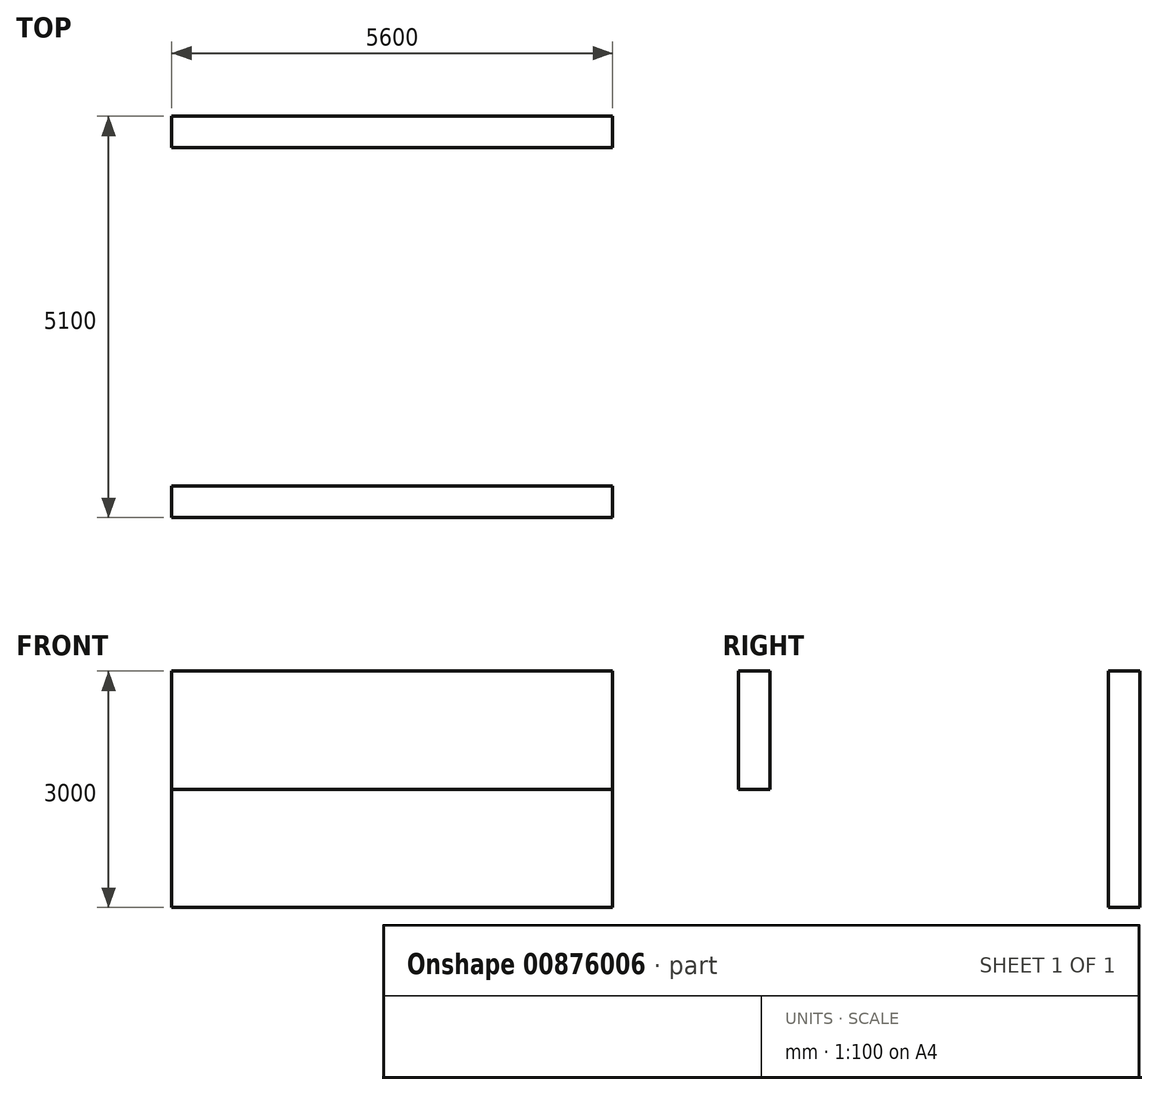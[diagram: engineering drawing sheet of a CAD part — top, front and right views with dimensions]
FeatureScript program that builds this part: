
annotation { "Feature Type Name" : "Feature", "Feature Type Description" : "" }
export const myFeature = defineFeature(function(context is Context, id is Id, definition is map)
    precondition{}
    {
        {
            var Q0;
            Q0=qCreatedBy(makeId("Top.planeOp"),FACE);
            var sketch = newSketch(context, id + "F0", { "sketchPlane" : qUnion([Q0])});
            skLineSegment(sketch, "E0", {"start": v(0, 0) * mm, "end": v(0, 5000) * mm});
            skLineSegment(sketch, "E1.bottom", {"start": v(-1500, 2550) * mm, "end": v(-7100, 2550) * mm});
            skLineSegment(sketch, "E1.top", {"start": v(-1500, -2550) * mm, "end": v(-7100, -2550) * mm});
            skLineSegment(sketch, "E1.left", {"start": v(-1500, 2550) * mm, "end": v(-1500, -2550) * mm});
            skLineSegment(sketch, "E1.right", {"start": v(-7100, 2550) * mm, "end": v(-7100, -2550) * mm});
            skLineSegment(sketch, "E2", {"start": v(0, 0) * mm, "end": v(0, -5000) * mm});
            skPoint(sketch, "E3", {"position": v(-1500, 0) * mm});
            skLineSegment(sketch, "E4", {"start": v(0, 0) * mm, "end": v(-8000, 0) * mm, "construction": true});
            skLineSegment(sketch, "E5", {"start": v(-7100, 2150) * mm, "end": v(-1500, 2150) * mm});
            skLineSegment(sketch, "E6", {"start": v(-7100, -2150) * mm, "end": v(-1500, -2150) * mm});
            skLineSegment(sketch, "E7", {"start": v(-3000, 2755) * mm, "end": v(-9573.95, 2755) * mm, "construction": true});
            skLineSegment(sketch, "E8", {"start": v(-3000, 2755) * mm, "end": v(-3000, 8624.5) * mm, "construction": true});
            skText(sketch, "E9", { "text": "Haus", "fontName": "OpenSans-Regular.ttf"});
            skLineSegment(sketch, "E10", {"start": v(-3000, 2755) * mm, "end": v(0, 2755) * mm, "construction": true});
            const initialGuessF0  = {"E9": [-6.08709, 3.80554, 1, 0, 0.54184]};
            skSetInitialGuess(sketch, initialGuessF0);
            skSolve(sketch);
        }
        {
            var Q0;
            {var subQ0=sQuery(id+"F0.wireOp",EDGE,"E1.top");Q0=makeQuery(id+"F0.imprint","IMPRINT",FACE,{"disambiguationData":[TD([[makeQuery(id+"F0.imprint","IMPRINT",EDGE,{"derivedFrom":subQ0}),-1.0]])]});}
            extrude(context, id + "F1", {"entities" : qUnion([Q0]), "oppositeDirection" : true, "depth" : 1500 * mm, "offsetDistance" : 25 * mm});
        }
        {
            var Q0;
            {var subQ0=sQuery(id+"F0.wireOp",EDGE,"E1.bottom");Q0=makeQuery(id+"F0.imprint","IMPRINT",FACE,{"disambiguationData":[TD([[makeQuery(id+"F0.imprint","IMPRINT",EDGE,{"derivedFrom":subQ0}),1.0]])]});}
            extrude(context, id + "F2", {"entities" : qUnion([Q0]), "oppositeDirection" : true, "depth" : 3000 * mm, "offsetDistance" : 25 * mm});
        }
        {
            var Q0;
            Q0=qCreatedBy(makeId("Right.planeOp"),FACE);
            var sketch = newSketch(context, id + "F3", { "sketchPlane" : qUnion([Q0])});
            skLineSegment(sketch, "E11", {"start": v(2755, 0) * mm, "end": v(2755, 325) * mm, "construction": true});
            skLineSegment(sketch, "E12", {"start": v(-2650, 0) * mm, "end": v(-2650, 175) * mm, "construction": true});
            skLineSegment(sketch, "E13", {"start": v(-2650, 175) * mm, "end": v(2755, 325) * mm});
            skPoint(sketch, "E14.0", {"position": v(-2550, 0) * mm});
            skLineSegment(sketch, "E15", {"start": v(-2550, 0) * mm, "end": v(-2550, 177.78) * mm, "construction": true});
            skLineSegment(sketch, "E16", {"start": v(0, 0) * mm, "end": v(0, 248.54) * mm, "construction": true});
            skLineSegment(sketch, "E17", {"start": v(0, 248.54) * mm, "end": v(0, 3048.54) * mm, "construction": true});
            skPoint(sketch, "E18.0", {"position": v(2550, 0) * mm});
            skLineSegment(sketch, "E19", {"start": v(2550, 0) * mm, "end": v(2550, 3500) * mm, "construction": true});
            skSolve(sketch);
        }
        {
            var Q0;
            Q0=makeQuery(id+"F2.opExtrude","SWEPT_FACE",FACE,{"disambiguationData":[OSD([sQuery(id+"F0.wireOp",EDGE,"E1.left")])]});
            var sketch = newSketch(context, id + "F4", { "sketchPlane" : qUnion([Q0])});
            skLineSegment(sketch, "E20", {"start": v(2550, 0) * mm, "end": v(2550, 400) * mm});
            skLineSegment(sketch, "E21", {"start": v(-2650, 0) * mm, "end": v(-2650, 400) * mm});
            skLineSegment(sketch, "E22.0", {"start": v(2755, 0) * mm, "end": v(2755, 400) * mm, "construction": true});
            skPoint(sketch, "E23.orphan", {"position": v(2755, 325) * mm});
            skLineSegment(sketch, "E24", {"start": v(2755, 400) * mm, "end": v(-2650, 400) * mm});
            skSolve(sketch);
        }
        {
            var Q0;
            Q0=makeQuery(id+"F1.opExtrude","SWEPT_FACE",FACE,{"disambiguationData":[OSD([sQuery(id+"F0.wireOp",EDGE,"E1.top")])]});
            cPlane(context, id + "F5", {"entities" : qUnion([Q0]), "cplaneType" : CPlaneType.OFFSET, "offset" : 100 * mm, "width" : 150 * mm, "height" : 150 * mm});
        }
        {
            var Q0;
            Q0=qCreatedBy(id+"F5.planeOp",FACE);
            var sketch = newSketch(context, id + "F6", { "sketchPlane" : qUnion([Q0])});
            skPoint(sketch, "E25.0", {"position": v(0, 177.78) * mm});
            skLineSegment(sketch, "E26.0", {"start": v(-1500, 0) * mm, "end": v(-7100, 0) * mm, "construction": true});
            skLineSegment(sketch, "E27", {"start": v(-1500, 0) * mm, "end": v(1749.53, -40.62) * mm, "construction": true});
            skLineSegment(sketch, "E28", {"start": v(-7100, 0) * mm, "end": v(-12930.36, 0) * mm, "construction": true});
            skLineSegment(sketch, "E29", {"start": v(-1500, 0) * mm, "end": v(-1500, 350) * mm});
            skLineSegment(sketch, "E30", {"start": v(-1500, 350) * mm, "end": v(0, 177.78) * mm});
            skLineSegment(sketch, "E31", {"start": v(-7100, 0) * mm, "end": v(-7100, 550) * mm});
            skLineSegment(sketch, "E32", {"start": v(-7100, 550) * mm, "end": v(-1500, 350) * mm});
            skLineSegment(sketch, "E33", {"start": v(0, 177.78) * mm, "end": v(0, -18.75) * mm, "construction": true});
            skPoint(sketch, "E34", {"position": v(0, -18.75) * mm});
            skSolve(sketch);
        }
        {
            var Q0;
            Q0=sQuery(id+"F3.wireOp",VERTEX,"E11.end");
            var Q1;
            Q1=sQuery(id+"F0.wireOp",VERTEX,"E10.end");
            var Q2;
            Q2=sQuery(id+"F0.wireOp",VERTEX,"E7.end");
            cPlane(context, id + "F7", {"entities" : qUnion([Q0, Q1, Q2]), "cplaneType" : CPlaneType.THREE_POINT, "offset" : 25 * mm, "width" : 150 * mm, "height" : 150 * mm});
        }
        {
            var Q0;
            Q0=qCreatedBy(id+"F7.planeOp",FACE);
            var sketch = newSketch(context, id + "F8", { "sketchPlane" : qUnion([Q0])});
            skPoint(sketch, "E35.0", {"position": v(0, 325) * mm});
            skLineSegment(sketch, "E36.0", {"start": v(-7100, -3000) * mm, "end": v(-7100, 0) * mm, "construction": true});
            skLineSegment(sketch, "E37.0", {"start": v(-1500, -3000) * mm, "end": v(-1500, 0) * mm, "construction": true});
            skLineSegment(sketch, "E38", {"start": v(-7100, 0) * mm, "end": v(-7100, 550) * mm, "construction": true});
            skLineSegment(sketch, "E39", {"start": v(-1500, 0) * mm, "end": v(-1500, 400) * mm, "construction": true});
            skLineSegment(sketch, "E40", {"start": v(-1500, 400) * mm, "end": v(-7100, 550) * mm});
            skSolve(sketch);
        }
        {
            var Q0;
            Q0=sQuery(id+"F4.wireOp",VERTEX,"E21.end");
            var Q1;
            {var subQ0=sQuery(id+"F0.wireOp",EDGE,"E1.top");Q1=makeQuery(id+"F0.imprint","IMPRINT",FACE,{"disambiguationData":[TD([[makeQuery(id+"F0.imprint","IMPRINT",EDGE,{"derivedFrom":subQ0}),-1.0]])]});}
            cPlane(context, id + "F9", {"entities" : qUnion([Q0, Q1]), "cplaneType" : CPlaneType.PLANE_POINT, "offset" : 25 * mm, "width" : 150 * mm, "height" : 150 * mm});
        }
        {
            var Q0;
            Q0=qCreatedBy(id+"F9.planeOp",FACE);
            var sketch = newSketch(context, id + "F10", { "sketchPlane" : qUnion([Q0])});
            skPoint(sketch, "E41.0", {"position": v(-7100, -2550) * mm});
            skPoint(sketch, "E42.0", {"position": v(-7100, 2550) * mm});
            skPoint(sketch, "E43.0", {"position": v(-1500, 2550) * mm});
            skPoint(sketch, "E44.0", {"position": v(-1500, -2550) * mm});
            skLineSegment(sketch, "E45", {"start": v(-7100, -2550) * mm, "end": v(-1500, -2550) * mm});
            skLineSegment(sketch, "E46", {"start": v(-1500, 2550) * mm, "end": v(-7100, 2550) * mm});
            skLineSegment(sketch, "E47", {"start": v(-7100, -2550) * mm, "end": v(-7100, 2550) * mm});
            skLineSegment(sketch, "E48", {"start": v(-1500, -2550) * mm, "end": v(-1500, 2550) * mm});
            skSolve(sketch);
        }
        {
            var Q0;
            Q0=sQuery(id+"F10.wireOp",EDGE,"E47");
            var Q1;
            Q1=sQuery(id+"F10.wireOp",EDGE,"E48");
            loft(context, id + "F11", {"bodyType" : ToolBodyType.SURFACE, "wireProfilesArray" : [{ "wireProfileEntities" : qUnion([Q0]) }, { "wireProfileEntities" : qUnion([Q1]) }]});
        }
        {
            var Q0;
            Q0=sQuery(id+"F8.wireOp",EDGE,"E40");
            var Q1;
            Q1=sQuery(id+"F6.wireOp",EDGE,"E32");
            loft(context, id + "F12", {"bodyType" : ToolBodyType.SURFACE, "wireProfilesArray" : [{ "wireProfileEntities" : qUnion([Q0]) }, { "wireProfileEntities" : qUnion([Q1]) }]});
        }
        {
            var Q0;
            Q0=sQuery(id+"F3.wireOp",EDGE,"E13");
            var Q1;
            Q1=makeQuery(id+"F12.opLoft","SWEPT_EDGE",EDGE,{"disambiguationData":[OSD([sQuery(id+"F6.wireOp",VERTEX,"E32.end"),sQuery(id+"F8.wireOp",VERTEX,"E40.start")])]});
            loft(context, id + "F13", {"bodyType" : ToolBodyType.SURFACE, "wireProfilesArray" : [{ "wireProfileEntities" : qUnion([Q0]) }, { "wireProfileEntities" : qUnion([Q1]) }]});
        }
    });
